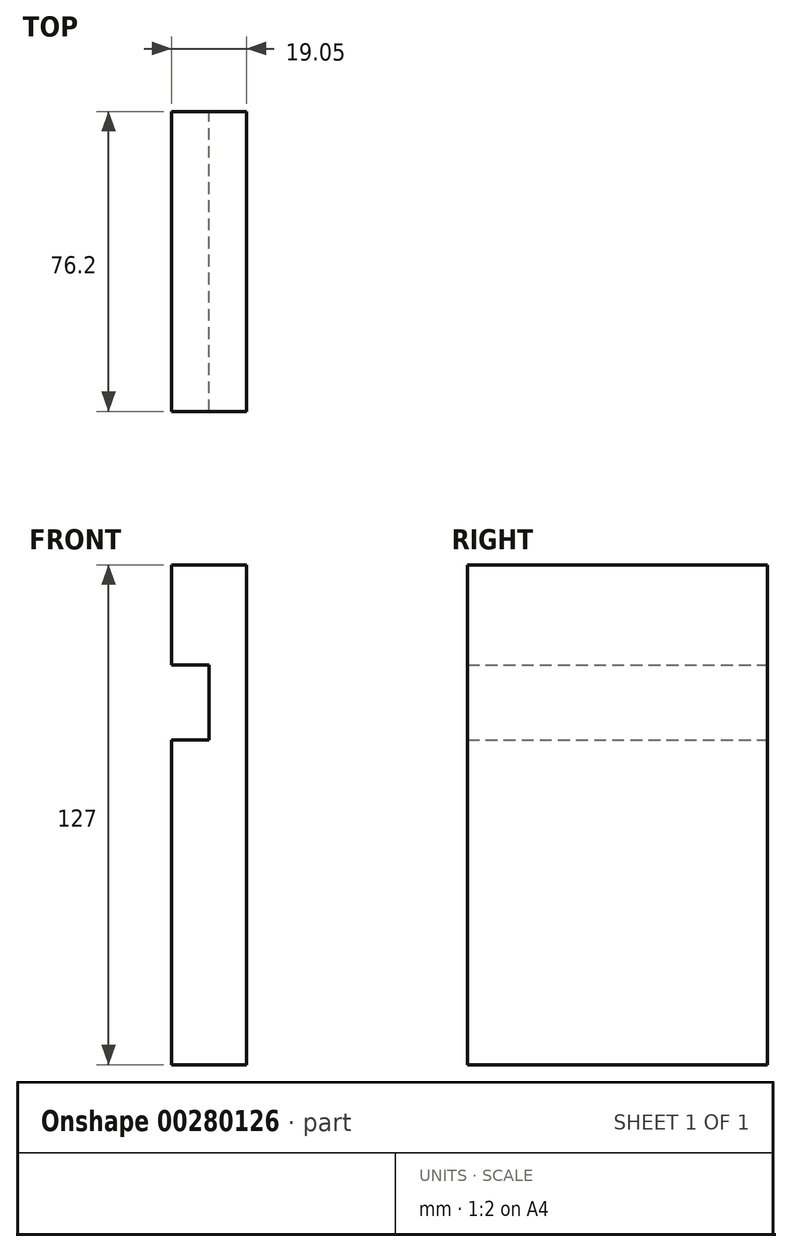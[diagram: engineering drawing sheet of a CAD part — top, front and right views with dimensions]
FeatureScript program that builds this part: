
annotation { "Feature Type Name" : "Feature", "Feature Type Description" : "" }
export const myFeature = defineFeature(function(context is Context, id is Id, definition is map)
    precondition{}
    {
        {
            var Q0;
            Q0=qCreatedBy(makeId("Front.planeOp"),FACE);
            var sketch = newSketch(context, id + "F0", { "sketchPlane" : qUnion([Q0])});
            skLineSegment(sketch, "E0", {"start": v(-22.77, 63.41) * mm, "end": v(-3.72, 63.41) * mm});
            skLineSegment(sketch, "E1", {"start": v(-3.72, 63.41) * mm, "end": v(-3.72, -63.59) * mm});
            skLineSegment(sketch, "E2", {"start": v(-3.72, -63.59) * mm, "end": v(-22.77, -63.59) * mm});
            skLineSegment(sketch, "E3", {"start": v(-22.77, 63.41) * mm, "end": v(-22.77, 38.01) * mm});
            skLineSegment(sketch, "E4", {"start": v(-22.77, 38.01) * mm, "end": v(-13.24, 38.01) * mm});
            skLineSegment(sketch, "E5", {"start": v(-13.24, 38.01) * mm, "end": v(-13.24, 18.96) * mm});
            skLineSegment(sketch, "E6", {"start": v(-13.24, 18.96) * mm, "end": v(-22.77, 18.96) * mm});
            skLineSegment(sketch, "E7", {"start": v(-22.77, 18.96) * mm, "end": v(-22.77, -63.59) * mm});
            skSolve(sketch);
        }
        {
            var Q0;
            Q0 = qSketchRegion(id + "F0", true);
            extrude(context, id + "F1", {"entities" : qUnion([Q0]), "depth" : 76.2 * mm});
        }
    });
